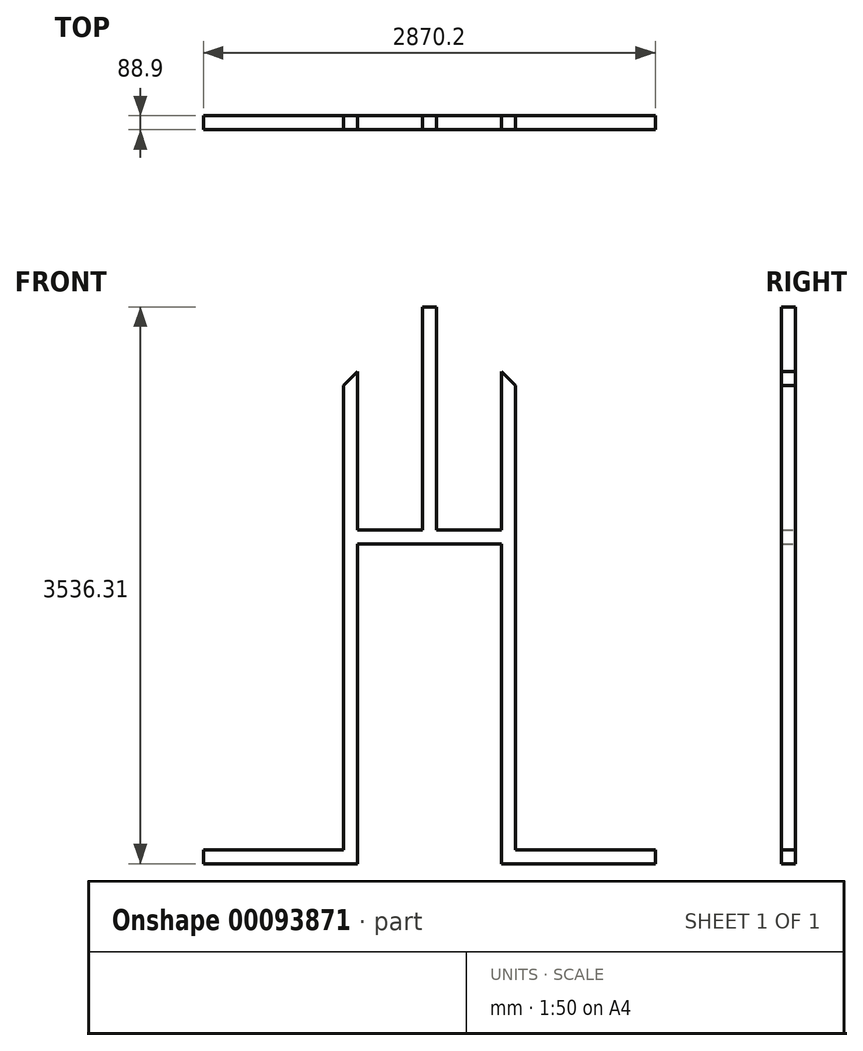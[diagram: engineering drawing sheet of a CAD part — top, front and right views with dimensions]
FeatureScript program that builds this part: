
annotation { "Feature Type Name" : "Feature", "Feature Type Description" : "" }
export const myFeature = defineFeature(function(context is Context, id is Id, definition is map)
    precondition{}
    {
        {
            var Q0;
            Q0=qCreatedBy(makeId("Front.planeOp"),FACE);
            var sketch = newSketch(context, id + "F0", { "sketchPlane" : qUnion([Q0])});
            skLineSegment(sketch, "E0.bottom", {"start": v(-1524, 0) * mm, "end": v(-1435.1, 0) * mm, "construction": true});
            skLineSegment(sketch, "E0.top", {"start": v(-1524, 2120.9) * mm, "end": v(-1435.1, 2120.9) * mm, "construction": true});
            skLineSegment(sketch, "E0.left", {"start": v(-1524, 0) * mm, "end": v(-1524, 2120.9) * mm, "construction": true});
            skLineSegment(sketch, "E0.right", {"start": v(1524, 0) * mm, "end": v(1524, 2120.9) * mm, "construction": true});
            skLineSegment(sketch, "E1", {"start": v(-457.2, 0) * mm, "end": v(-457.2, 2032) * mm});
            skLineSegment(sketch, "E2", {"start": v(-457.2, 2032) * mm, "end": v(457.2, 2032) * mm});
            skLineSegment(sketch, "E3", {"start": v(457.2, 2032) * mm, "end": v(457.2, 0) * mm});
            skLineSegment(sketch, "E4", {"start": v(-1524, 2120.9) * mm, "end": v(0, 3644.9) * mm, "construction": true});
            skLineSegment(sketch, "E5", {"start": v(0, 3644.9) * mm, "end": v(1524, 2120.9) * mm, "construction": true});
            skLineSegment(sketch, "E6", {"start": v(-546.1, 88.9) * mm, "end": v(-546.1, 3035.94) * mm});
            skLineSegment(sketch, "E7", {"start": v(546.1, 88.9) * mm, "end": v(546.1, 3035.94) * mm});
            skLineSegment(sketch, "E8", {"start": v(-457.2, 2120.9) * mm, "end": v(-44.45, 2120.9) * mm});
            skLineSegment(sketch, "E9", {"start": v(457.2, 2120.9) * mm, "end": v(457.2, 3124.84) * mm});
            skLineSegment(sketch, "E10", {"start": v(-1435.1, 2120.9) * mm, "end": v(-1435.1, 88.9) * mm, "construction": true});
            skLineSegment(sketch, "E11", {"start": v(-1435.1, 88.9) * mm, "end": v(-546.1, 88.9) * mm});
            skLineSegment(sketch, "E12", {"start": v(1435.1, 2120.9) * mm, "end": v(1435.1, 88.9) * mm, "construction": true});
            skLineSegment(sketch, "E13", {"start": v(1435.1, 88.9) * mm, "end": v(546.1, 88.9) * mm});
            skLineSegment(sketch, "E14.trimOffspring", {"start": v(1435.1, 2120.9) * mm, "end": v(1524, 2120.9) * mm, "construction": true});
            skLineSegment(sketch, "E15", {"start": v(1435.1, 0) * mm, "end": v(1524, 0) * mm, "construction": true});
            skLineSegment(sketch, "E16", {"start": v(-1435.1, 0) * mm, "end": v(-457.2, 0) * mm});
            skLineSegment(sketch, "E17", {"start": v(-1435.1, 88.9) * mm, "end": v(-1435.1, 0) * mm});
            skLineSegment(sketch, "E18", {"start": v(1435.1, 88.9) * mm, "end": v(1435.1, 0) * mm});
            skLineSegment(sketch, "E19", {"start": v(-457.2, 0) * mm, "end": v(457.2, 0) * mm, "construction": true});
            skLineSegment(sketch, "E20", {"start": v(457.2, 0) * mm, "end": v(1435.1, 0) * mm});
            skLineSegment(sketch, "E21", {"start": v(0, 3644.9) * mm, "end": v(0, 0) * mm, "construction": true});
            skLineSegment(sketch, "E22", {"start": v(-44.45, 2120.9) * mm, "end": v(44.45, 2120.9) * mm, "construction": true});
            skLineSegment(sketch, "E23", {"start": v(44.45, 2120.9) * mm, "end": v(457.2, 2120.9) * mm});
            skLineSegment(sketch, "E24", {"start": v(-1467.17, 2114.87) * mm, "end": v(-546.1, 3035.94) * mm, "construction": true});
            skLineSegment(sketch, "E25", {"start": v(1461.14, 2120.9) * mm, "end": v(0, 3582.04) * mm, "construction": true});
            skLineSegment(sketch, "E26", {"start": v(44.45, 3536.31) * mm, "end": v(44.45, 2120.9) * mm});
            skLineSegment(sketch, "E27.trimOffspring", {"start": v(-457.2, 3124.84) * mm, "end": v(0, 3582.04) * mm, "construction": true});
            skLineSegment(sketch, "E28", {"start": v(-546.1, 3035.94) * mm, "end": v(-457.2, 3124.84) * mm});
            skLineSegment(sketch, "E29", {"start": v(-457.2, 3124.84) * mm, "end": v(-457.2, 2120.9) * mm});
            skLineSegment(sketch, "E30", {"start": v(457.2, 3124.84) * mm, "end": v(546.1, 3035.94) * mm});
            skLineSegment(sketch, "E31.top", {"start": v(-44.45, 3536.31) * mm, "end": v(44.45, 3536.31) * mm});
            skLineSegment(sketch, "E32", {"start": v(-44.45, 2120.9) * mm, "end": v(-44.45, 3536.31) * mm});
            skLineSegment(sketch, "E33", {"start": v(0, 3707.76) * mm, "end": v(-1249.26, 2458.5) * mm, "construction": true});
            skLineSegment(sketch, "E34", {"start": v(-44.45, 3536.31) * mm, "end": v(-44.45, 3663.31) * mm, "construction": true});
            skLineSegment(sketch, "E35", {"start": v(44.45, 3536.31) * mm, "end": v(44.45, 3663.31) * mm, "construction": true});
            skLineSegment(sketch, "E36", {"start": v(-44.45, 3663.31) * mm, "end": v(44.45, 3663.31) * mm, "construction": true});
            skSolve(sketch);
        }
        {
            var Q0;
            Q0 = qSketchRegion(id + "F0", true);
            extrude(context, id + "F1", {"entities" : qUnion([Q0]), "depth" : 88.9 * mm});
        }
    });
